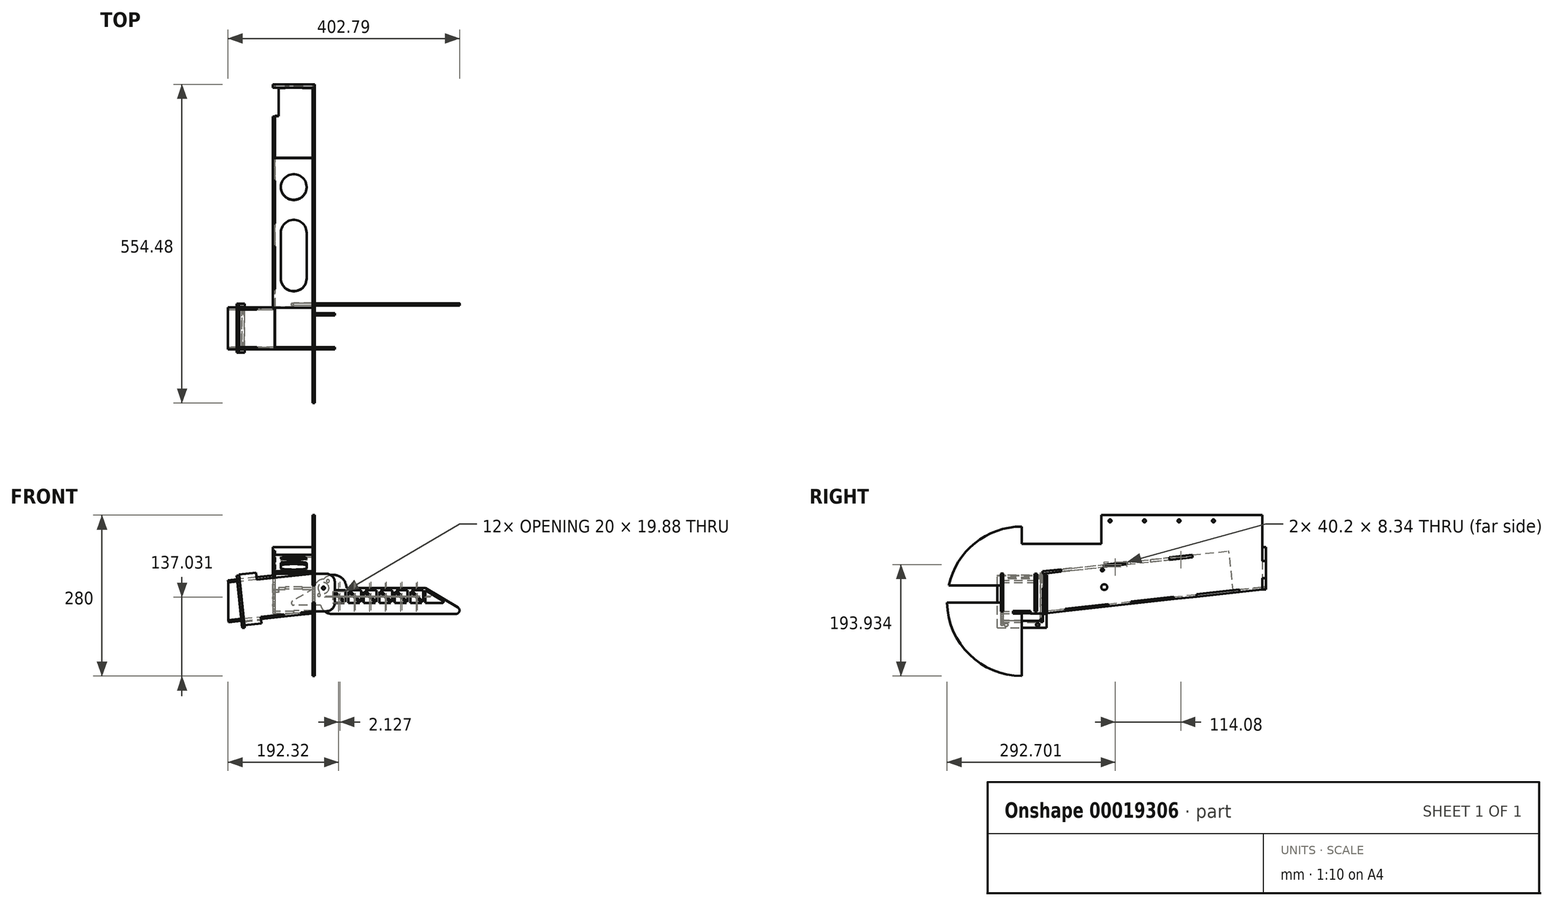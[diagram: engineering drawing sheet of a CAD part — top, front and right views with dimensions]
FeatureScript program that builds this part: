
annotation { "Feature Type Name" : "Feature", "Feature Type Description" : "" }
export const myFeature = defineFeature(function(context is Context, id is Id, definition is map)
    precondition{}
    {
        {
            var Q0;
            Q0=qCreatedBy(makeId("Front.planeOp"),FACE);
            var sketch = newSketch(context, id + "F0", { "sketchPlane" : qUnion([Q0])});
            skCircle(sketch, "E0", {"center": v(0, 0) * mm, "radius": 150 * mm, "construction": true});
            skLineSegment(sketch, "E1", {"start": v(0, 150) * mm, "end": v(0, -150) * mm, "construction": true});
            skSolve(sketch);
        }
        {
            var Q0;
            Q0=qCreatedBy(makeId("Front.planeOp"),FACE);
            var sketch = newSketch(context, id + "F1", { "sketchPlane" : qUnion([Q0])});
            skLineSegment(sketch, "E2", {"start": v(-146.4, 32.68) * mm, "end": v(-146.4, -32.68) * mm});
            skLineSegment(sketch, "E3", {"start": v(-146.4, -32.68) * mm, "end": v(-119.71, -29.87) * mm});
            skLineSegment(sketch, "E4", {"start": v(0, -17.3) * mm, "end": v(0, -2.3) * mm});
            skLineSegment(sketch, "E5", {"start": v(0, 48.07) * mm, "end": v(-96.67, 37.9) * mm});
            skLineSegment(sketch, "E6.bottom", {"start": v(0, -17.3) * mm, "end": v(-73, -17.3) * mm, "construction": true});
            skLineSegment(sketch, "E6.top", {"start": v(0, 48.07) * mm, "end": v(-73, 48.07) * mm, "construction": true});
            skLineSegment(sketch, "E6.left", {"start": v(0, -17.3) * mm, "end": v(0, 48.07) * mm, "construction": true});
            skLineSegment(sketch, "E6.right", {"start": v(-73, -17.3) * mm, "end": v(-73, 48.07) * mm, "construction": true});
            skLineSegment(sketch, "E7", {"start": v(-119.71, -29.87) * mm, "end": v(-118.46, -41.8) * mm});
            skLineSegment(sketch, "E8", {"start": v(-118.46, -41.8) * mm, "end": v(-88.62, -38.67) * mm});
            skLineSegment(sketch, "E9", {"start": v(-88.62, -38.67) * mm, "end": v(-89.88, -26.74) * mm});
            skLineSegment(sketch, "E10", {"start": v(-49.73, -22.52) * mm, "end": v(-49.3, -26.5) * mm});
            skLineSegment(sketch, "E11", {"start": v(-49.3, -26.5) * mm, "end": v(-19.47, -23.36) * mm});
            skLineSegment(sketch, "E12", {"start": v(-19.47, -23.36) * mm, "end": v(-19.9, -19.38) * mm});
            skLineSegment(sketch, "E13", {"start": v(-126.5, 34.77) * mm, "end": v(-127.76, 46.7) * mm});
            skLineSegment(sketch, "E14", {"start": v(-127.76, 46.7) * mm, "end": v(-97.93, 49.84) * mm});
            skLineSegment(sketch, "E15", {"start": v(-97.93, 49.84) * mm, "end": v(-96.67, 37.9) * mm});
            skLineSegment(sketch, "E16", {"start": v(0, 27.7) * mm, "end": v(4, 27.7) * mm});
            skLineSegment(sketch, "E17", {"start": v(4, -2.3) * mm, "end": v(0, -2.3) * mm});
            skLineSegment(sketch, "E18", {"start": v(-146.4, 32.68) * mm, "end": v(-139.6, -31.96) * mm, "construction": true});
            skLineSegment(sketch, "E19.trimOffspring", {"start": v(-89.88, -26.74) * mm, "end": v(-49.73, -22.52) * mm});
            skLineSegment(sketch, "E20.trimOffspring", {"start": v(-126.5, 34.77) * mm, "end": v(-146.4, 32.68) * mm});
            skLineSegment(sketch, "E21.trimOffspring", {"start": v(-19.9, -19.38) * mm, "end": v(0, -17.3) * mm});
            skLineSegment(sketch, "E22.trimOffspring", {"start": v(0, 27.7) * mm, "end": v(0, 48.07) * mm});
            skLineSegment(sketch, "E23.bottom", {"start": v(4, 48.07) * mm, "end": v(24, 48.07) * mm});
            skLineSegment(sketch, "E23.top", {"start": v(4, -17.3) * mm, "end": v(24, -17.3) * mm});
            skLineSegment(sketch, "E23.left", {"start": v(4, 48.07) * mm, "end": v(4, 27.7) * mm});
            skLineSegment(sketch, "E23.right", {"start": v(39, 33.07) * mm, "end": v(39, -2.3) * mm});
            skLineSegment(sketch, "E24.trimOffspring", {"start": v(4, -2.3) * mm, "end": v(4, -17.3) * mm});
            skCircle(sketch, "E25", {"center": v(19.25, 23.09) * mm, "radius": 2.5 * mm});
            skPoint(sketch, "E26.visualSharp", {"position": v(39, 48.07) * mm});
            skArc(sketch, "E26.filletArc", {"start": v(39, 33.07) * mm, "mid": v(34.6, 43.67) * mm, "end": v(24, 48.07) * mm});
            skPoint(sketch, "E27.visualSharp", {"position": v(39, -17.3) * mm});
            skArc(sketch, "E27.filletArc", {"start": v(24, -17.3) * mm, "mid": v(34.6, -12.9) * mm, "end": v(39, -2.3) * mm});
            skSolve(sketch);
        }
        {
            var Q0;
            Q0=qSketchRegion(id+"F1",true);
            extrude(context, id + "F2", {"entities" : qUnion([Q0]), "depth" : 4 * mm});
        }
        {
            var Q0;
            Q0=makeQuery(id+"F2.opExtrude","SWEPT_FACE",FACE,{"disambiguationData":[OSD([sQuery(id+"F1.wireOp",EDGE,"E3")])]});
            var sketch = newSketch(context, id + "F3", { "sketchPlane" : qUnion([Q0])});
            skLineSegment(sketch, "E28.bottom", {"start": v(-149.01, 4) * mm, "end": v(-122.18, 4) * mm});
            skLineSegment(sketch, "E28.top", {"start": v(-149.01, -69) * mm, "end": v(-122.18, -69) * mm});
            skLineSegment(sketch, "E28.left", {"start": v(-149.01, 4) * mm, "end": v(-149.01, -69) * mm});
            skLineSegment(sketch, "E28.right", {"start": v(-1.8, 4) * mm, "end": v(-1.8, -17.5) * mm});
            skLineSegment(sketch, "E29", {"start": v(-122.18, 4) * mm, "end": v(-122.18, 0) * mm});
            skLineSegment(sketch, "E30", {"start": v(-122.18, 0) * mm, "end": v(-92.18, 0) * mm});
            skLineSegment(sketch, "E31", {"start": v(-92.18, 0) * mm, "end": v(-92.18, 4) * mm});
            skLineSegment(sketch, "E32.0.0", {"start": v(-51.8, 0) * mm, "end": v(-21.8, 0) * mm});
            skLineSegment(sketch, "E32.0.1", {"start": v(-21.8, 0) * mm, "end": v(-21.8, 4) * mm});
            skLineSegment(sketch, "E32.0.3", {"start": v(-51.8, 4) * mm, "end": v(-51.8, 0) * mm});
            skLineSegment(sketch, "E33.trimOffspring", {"start": v(-21.8, 4) * mm, "end": v(-1.8, 4) * mm});
            skLineSegment(sketch, "E34.trimOffspring", {"start": v(-92.18, 4) * mm, "end": v(-51.8, 4) * mm});
            skLineSegment(sketch, "E35", {"start": v(-1.8, -17.5) * mm, "end": v(2.2, -17.5) * mm});
            skLineSegment(sketch, "E36", {"start": v(2.2, -17.5) * mm, "end": v(2.2, -47.5) * mm});
            skLineSegment(sketch, "E37", {"start": v(2.2, -47.5) * mm, "end": v(-1.8, -47.5) * mm});
            skLineSegment(sketch, "E38.trimOffspring", {"start": v(-1.8, -47.5) * mm, "end": v(-1.8, -69) * mm});
            skLineSegment(sketch, "E39", {"start": v(-122.18, -69) * mm, "end": v(-122.18, -65) * mm});
            skLineSegment(sketch, "E40", {"start": v(-122.18, -65) * mm, "end": v(-92.18, -65) * mm});
            skLineSegment(sketch, "E41", {"start": v(-92.18, -65) * mm, "end": v(-92.18, -69) * mm});
            skLineSegment(sketch, "E42.trimOffspring", {"start": v(-92.18, -69) * mm, "end": v(-1.8, -69) * mm});
            skSolve(sketch);
        }
        {
            var Q0;
            Q0=qSketchRegion(id+"F3",true);
            extrude(context, id + "F4", {"entities" : qUnion([Q0]), "depth" : 4 * mm});
        }
        {
            var Q0;
            Q0=makeQuery(id+"F2.opExtrude","SWEPT_FACE",FACE,{"disambiguationData":[OSD([sQuery(id+"F1.wireOp",EDGE,"E22.trimOffspring")])]});
            var sketch = newSketch(context, id + "F5", { "sketchPlane" : qUnion([Q0])});
            skLineSegment(sketch, "E43", {"start": v(451, 20.66) * mm, "end": v(451, 40.33) * mm});
            skLineSegment(sketch, "E44", {"start": v(451, 90) * mm, "end": v(403.72, 84.8) * mm});
            skLineSegment(sketch, "E45", {"start": v(69, 48.07) * mm, "end": v(-4, 48.07) * mm, "construction": true});
            skLineSegment(sketch, "E46", {"start": v(-4, 27.7) * mm, "end": v(0, 27.7) * mm});
            skLineSegment(sketch, "E47", {"start": v(0, 27.7) * mm, "end": v(0, -2.3) * mm});
            skLineSegment(sketch, "E48", {"start": v(0, -2.3) * mm, "end": v(-4, -2.3) * mm});
            skLineSegment(sketch, "E49", {"start": v(17.5, -21.27) * mm, "end": v(17.5, -16.87) * mm});
            skLineSegment(sketch, "E50", {"start": v(17.5, -16.87) * mm, "end": v(47.5, -16.87) * mm});
            skLineSegment(sketch, "E51", {"start": v(47.5, -16.87) * mm, "end": v(47.5, -21.27) * mm});
            skLineSegment(sketch, "E52", {"start": v(47.5, -21.27) * mm, "end": v(69, -21.27) * mm});
            skLineSegment(sketch, "E53", {"start": v(32.5, 48.07) * mm, "end": v(32.5, -16.87) * mm, "construction": true});
            skCircle(sketch, "E54", {"center": v(32.5, 0) * mm, "radius": 150 * mm, "construction": true});
            skLineSegment(sketch, "E55", {"start": v(-117.5, 0) * mm, "end": v(-117.5, -150) * mm, "construction": true});
            skLineSegment(sketch, "E56", {"start": v(-117.5, -150) * mm, "end": v(451, -150) * mm, "construction": true});
            skLineSegment(sketch, "E57", {"start": v(451, -150) * mm, "end": v(451, 150) * mm, "construction": true});
            skLineSegment(sketch, "E58", {"start": v(451, 150) * mm, "end": v(-117.5, 150) * mm, "construction": true});
            skLineSegment(sketch, "E59", {"start": v(-117.5, 0) * mm, "end": v(-117.5, 150) * mm, "construction": true});
            skLineSegment(sketch, "E60", {"start": v(451, 70.33) * mm, "end": v(457, 70.33) * mm});
            skLineSegment(sketch, "E61", {"start": v(457, 70.33) * mm, "end": v(457, 40.33) * mm});
            skLineSegment(sketch, "E62", {"start": v(457, 40.33) * mm, "end": v(451, 40.33) * mm});
            skLineSegment(sketch, "E63.trimOffspring", {"start": v(451, 70.33) * mm, "end": v(451, 90) * mm});
            skLineSegment(sketch, "E64", {"start": v(108.76, -16.9) * mm, "end": v(108.32, -12.93) * mm});
            skLineSegment(sketch, "E65", {"start": v(108.32, -12.93) * mm, "end": v(182.64, -4.77) * mm});
            skLineSegment(sketch, "E66", {"start": v(182.64, -4.77) * mm, "end": v(183.08, -8.75) * mm});
            skLineSegment(sketch, "E67", {"start": v(222.84, -4.38) * mm, "end": v(222.4, -0.4) * mm});
            skLineSegment(sketch, "E68", {"start": v(222.4, -0.4) * mm, "end": v(296.72, 7.75) * mm});
            skLineSegment(sketch, "E69", {"start": v(296.72, 7.75) * mm, "end": v(297.16, 3.78) * mm});
            skLineSegment(sketch, "E70", {"start": v(336.92, 8.14) * mm, "end": v(336.48, 12.12) * mm});
            skLineSegment(sketch, "E71", {"start": v(336.48, 12.12) * mm, "end": v(410.8, 20.28) * mm});
            skLineSegment(sketch, "E72", {"start": v(410.8, 20.28) * mm, "end": v(411.24, 16.3) * mm});
            skLineSegment(sketch, "E73.trimOffspring", {"start": v(183.08, -8.75) * mm, "end": v(222.84, -4.38) * mm});
            skLineSegment(sketch, "E74.trimOffspring", {"start": v(411.24, 16.3) * mm, "end": v(451, 20.66) * mm});
            skLineSegment(sketch, "E75", {"start": v(108.76, -16.9) * mm, "end": v(76, -20.5) * mm});
            skLineSegment(sketch, "E76.trimOffspring", {"start": v(297.16, 3.78) * mm, "end": v(336.92, 8.14) * mm});
            skLineSegment(sketch, "E77", {"start": v(101.24, 51.6) * mm, "end": v(100.8, 55.58) * mm});
            skLineSegment(sketch, "E78", {"start": v(100.8, 55.58) * mm, "end": v(175.12, 63.74) * mm, "construction": true});
            skLineSegment(sketch, "E79", {"start": v(175.12, 63.74) * mm, "end": v(175.56, 59.76) * mm});
            skLineSegment(sketch, "E80", {"start": v(215.32, 64.13) * mm, "end": v(214.88, 68.1) * mm});
            skLineSegment(sketch, "E81", {"start": v(214.88, 68.1) * mm, "end": v(289.2, 76.26) * mm, "construction": true});
            skLineSegment(sketch, "E82", {"start": v(289.2, 76.26) * mm, "end": v(289.64, 72.29) * mm});
            skLineSegment(sketch, "E83", {"start": v(329.4, 76.65) * mm, "end": v(328.96, 80.63) * mm});
            skLineSegment(sketch, "E84", {"start": v(328.96, 80.63) * mm, "end": v(403.28, 88.79) * mm, "construction": true});
            skLineSegment(sketch, "E85", {"start": v(403.28, 88.79) * mm, "end": v(403.72, 84.8) * mm});
            skLineSegment(sketch, "E86.trimOffspring", {"start": v(101.24, 51.6) * mm, "end": v(69, 48.07) * mm});
            skLineSegment(sketch, "E87.trimOffspring", {"start": v(215.32, 64.13) * mm, "end": v(175.56, 59.76) * mm});
            skLineSegment(sketch, "E88.trimOffspring", {"start": v(329.4, 76.65) * mm, "end": v(289.64, 72.29) * mm});
            skLineSegment(sketch, "E89.bottom", {"start": v(69, 22.81) * mm, "end": v(76, 22.81) * mm});
            skLineSegment(sketch, "E89.top", {"start": v(69, -7.19) * mm, "end": v(76, -7.19) * mm, "construction": true});
            skLineSegment(sketch, "E89.left", {"start": v(69, 22.81) * mm, "end": v(69, -7.19) * mm});
            skLineSegment(sketch, "E89.right", {"start": v(76, 22.81) * mm, "end": v(76, -7.19) * mm});
            skLineSegment(sketch, "E90", {"start": v(76, -7.19) * mm, "end": v(76, -20.5) * mm});
            skLineSegment(sketch, "E91", {"start": v(69, -7.19) * mm, "end": v(69, -21.27) * mm});
            skLineSegment(sketch, "E92.trimOffspring", {"start": v(69, -21.27) * mm, "end": v(69, -21.27) * mm});
            skLineSegment(sketch, "E93", {"start": v(451, 90) * mm, "end": v(451, 150) * mm});
            skLineSegment(sketch, "E94", {"start": v(451, 150) * mm, "end": v(-4, 150) * mm, "construction": true});
            skLineSegment(sketch, "E95", {"start": v(-4, 48.07) * mm, "end": v(-4, 150) * mm, "construction": true});
            skLineSegment(sketch, "E96", {"start": v(175.12, 63.74) * mm, "end": v(214.88, 68.1) * mm});
            skLineSegment(sketch, "E97", {"start": v(289.2, 76.26) * mm, "end": v(328.96, 80.63) * mm});
            skLineSegment(sketch, "E98", {"start": v(403.28, 88.79) * mm, "end": v(451, 94.02) * mm});
            skLineSegment(sketch, "E99", {"start": v(69, 48.07) * mm, "end": v(68.56, 52.04) * mm});
            skLineSegment(sketch, "E100", {"start": v(68.56, 52.04) * mm, "end": v(100.8, 55.58) * mm});
            skCircle(sketch, "E101", {"center": v(66, 140) * mm, "radius": 2.5 * mm, "construction": true});
            skCircle(sketch, "E102", {"center": v(126, 140) * mm, "radius": 2.5 * mm, "construction": true});
            skCircle(sketch, "E103", {"center": v(186, 140) * mm, "radius": 2.5 * mm});
            skCircle(sketch, "E104", {"center": v(246, 140) * mm, "radius": 2.5 * mm});
            skCircle(sketch, "E105", {"center": v(306, 140) * mm, "radius": 2.5 * mm});
            skCircle(sketch, "E106", {"center": v(366, 140) * mm, "radius": 2.5 * mm});
            skCircle(sketch, "E107", {"center": v(421, 120) * mm, "radius": 30 * mm, "construction": true});
            skLineSegment(sketch, "E108.bottom", {"start": v(55, 40.73) * mm, "end": v(59, 40.73) * mm});
            skLineSegment(sketch, "E108.top", {"start": v(55, 20.73) * mm, "end": v(59, 20.73) * mm});
            skLineSegment(sketch, "E108.left", {"start": v(55, 40.73) * mm, "end": v(55, 20.73) * mm});
            skLineSegment(sketch, "E108.right", {"start": v(59, 40.73) * mm, "end": v(59, 20.73) * mm});
            skLineSegment(sketch, "E109.bottom", {"start": v(55, 12.73) * mm, "end": v(59, 12.73) * mm});
            skLineSegment(sketch, "E109.top", {"start": v(55, -7.27) * mm, "end": v(59, -7.27) * mm});
            skLineSegment(sketch, "E109.left", {"start": v(55, 12.73) * mm, "end": v(55, -7.27) * mm});
            skLineSegment(sketch, "E109.right", {"start": v(59, 12.73) * mm, "end": v(59, -7.27) * mm});
            skLineSegment(sketch, "E110", {"start": v(-4, 100) * mm, "end": v(171, 100) * mm});
            skLineSegment(sketch, "E111", {"start": v(171, 100) * mm, "end": v(171, 150) * mm});
            skLineSegment(sketch, "E112", {"start": v(171, 150) * mm, "end": v(451, 150) * mm});
            skArc(sketch, "E113", {"start": v(32.5, 130) * mm, "mid": v(-49.04, 101.25) * mm, "end": v(-94.51, 27.7) * mm});
            skLineSegment(sketch, "E114", {"start": v(32.5, 130) * mm, "end": v(32.5, -130) * mm, "construction": true});
            skLineSegment(sketch, "E115", {"start": v(32.5, 130) * mm, "end": v(32.5, 100) * mm});
            skLineSegment(sketch, "E116", {"start": v(32.5, -130) * mm, "end": v(32.5, -21.27) * mm});
            skLineSegment(sketch, "E117", {"start": v(32.5, -21.27) * mm, "end": v(17.5, -21.27) * mm});
            skLineSegment(sketch, "E118", {"start": v(-4, 27.7) * mm, "end": v(-94.51, 27.7) * mm});
            skLineSegment(sketch, "E119", {"start": v(-4, -2.3) * mm, "end": v(-97.48, -2.3) * mm});
            skArc(sketch, "E120.trimOffspring", {"start": v(-97.48, -2.3) * mm, "mid": v(-58.6, -92.73) * mm, "end": v(32.5, -130) * mm});
            skLineSegment(sketch, "E121", {"start": v(76, 13.7) * mm, "end": v(176, 24.68) * mm, "construction": true});
            skCircle(sketch, "E122", {"center": v(176, 24.68) * mm, "radius": 5 * mm});
            skLineSegment(sketch, "E123", {"start": v(172.73, 54.5) * mm, "end": v(176, 24.68) * mm, "construction": true});
            skCircle(sketch, "E124", {"center": v(172.73, 54.5) * mm, "radius": 2.5 * mm});
            skSolve(sketch);
        }
        {
            var Q0;
            Q0=qSketchRegion(id+"F5",true);
            extrude(context, id + "F6", {"entities" : qUnion([Q0]), "depth" : 4 * mm});
        }
        {
            var Q0;
            Q0=makeQuery(id+"F6.opExtrude","SWEPT_FACE",FACE,{"disambiguationData":[OSD([sQuery(id+"F5.wireOp",EDGE,"E68")])]});
            var sketch = newSketch(context, id + "F7", { "sketchPlane" : qUnion([Q0])});
            skLineSegment(sketch, "E125", {"start": v(-65, -66.7) * mm, "end": v(-65, -106.27) * mm});
            skLineSegment(sketch, "E126", {"start": v(-65, -450.56) * mm, "end": v(-47.5, -450.56) * mm});
            skLineSegment(sketch, "E127", {"start": v(4, -410.56) * mm, "end": v(4, -335.8) * mm});
            skLineSegment(sketch, "E128.0.0", {"start": v(0, -410.56) * mm, "end": v(0, -450.56) * mm});
            skLineSegment(sketch, "E128.0.3", {"start": v(4, -410.56) * mm, "end": v(0, -410.56) * mm});
            skPoint(sketch, "E128.0.1.end.orphan", {"position": v(4, -450.56) * mm});
            skLineSegment(sketch, "E129.0.0", {"start": v(0, -295.8) * mm, "end": v(0, -335.8) * mm});
            skLineSegment(sketch, "E129.0.1", {"start": v(0, -335.8) * mm, "end": v(4, -335.8) * mm});
            skLineSegment(sketch, "E129.0.3", {"start": v(4, -295.8) * mm, "end": v(0, -295.8) * mm});
            skLineSegment(sketch, "E130.trimOffspring", {"start": v(4, -295.8) * mm, "end": v(4, -221.03) * mm});
            skLineSegment(sketch, "E131.0.0", {"start": v(0, -181.03) * mm, "end": v(0, -221.03) * mm});
            skLineSegment(sketch, "E131.0.1", {"start": v(0, -221.03) * mm, "end": v(4, -221.03) * mm});
            skLineSegment(sketch, "E131.0.3", {"start": v(4, -181.03) * mm, "end": v(0, -181.03) * mm});
            skLineSegment(sketch, "E132.trimOffspring", {"start": v(4, -181.03) * mm, "end": v(4, -106.27) * mm});
            skLineSegment(sketch, "E133.0.0", {"start": v(0, -66.7) * mm, "end": v(0, -67.8) * mm});
            skLineSegment(sketch, "E133.0.1", {"start": v(0, -106.27) * mm, "end": v(4, -106.27) * mm});
            skLineSegment(sketch, "E134", {"start": v(0, -66.7) * mm, "end": v(-65, -66.7) * mm});
            skLineSegment(sketch, "E135", {"start": v(-32.5, -450.56) * mm, "end": v(-32.5, -66.7) * mm, "construction": true});
            skLineSegment(sketch, "E136.0.MirrorCS", {"start": v(-65, -106.27) * mm, "end": v(-69, -106.27) * mm});
            skLineSegment(sketch, "E137.0.MirrorCS", {"start": v(-69, -181.03) * mm, "end": v(-69, -106.27) * mm});
            skLineSegment(sketch, "E138.0.MirrorCS", {"start": v(-69, -181.03) * mm, "end": v(-65, -181.03) * mm});
            skLineSegment(sketch, "E139.0.MirrorCS", {"start": v(-65, -221.03) * mm, "end": v(-69, -221.03) * mm});
            skLineSegment(sketch, "E140.0.MirrorCS", {"start": v(-69, -295.8) * mm, "end": v(-69, -221.03) * mm});
            skLineSegment(sketch, "E141.0.MirrorCS", {"start": v(-69, -295.8) * mm, "end": v(-65, -295.8) * mm});
            skLineSegment(sketch, "E142.0.MirrorCS", {"start": v(-65, -335.8) * mm, "end": v(-69, -335.8) * mm});
            skLineSegment(sketch, "E143.0.MirrorCS", {"start": v(-69, -396.56) * mm, "end": v(-69, -335.8) * mm});
            skLineSegment(sketch, "E144.trimOffspring", {"start": v(-65, -181.03) * mm, "end": v(-65, -221.03) * mm});
            skLineSegment(sketch, "E145.trimOffspring", {"start": v(-65, -295.8) * mm, "end": v(-65, -335.8) * mm});
            skLineSegment(sketch, "E146.trimOffspring", {"start": v(-65, -440.56) * mm, "end": v(-65, -450.56) * mm});
            skLineSegment(sketch, "E147", {"start": v(-17.5, -450.56) * mm, "end": v(-17.5, -454.56) * mm});
            skLineSegment(sketch, "E148", {"start": v(-17.5, -454.56) * mm, "end": v(-47.5, -454.56) * mm});
            skLineSegment(sketch, "E149", {"start": v(-47.5, -454.56) * mm, "end": v(-47.5, -450.56) * mm});
            skLineSegment(sketch, "E150.trimOffspring", {"start": v(-17.5, -450.56) * mm, "end": v(0, -450.56) * mm});
            skLineSegment(sketch, "E151.bottom", {"start": v(0, -67.8) * mm, "end": v(-32.5, -67.8) * mm});
            skLineSegment(sketch, "E151.top", {"start": v(0, -73.8) * mm, "end": v(-32.5, -73.8) * mm});
            skLineSegment(sketch, "E151.right", {"start": v(-32.5, -67.8) * mm, "end": v(-32.5, -73.8) * mm});
            skLineSegment(sketch, "E152.trimOffspring", {"start": v(0, -73.8) * mm, "end": v(0, -106.27) * mm});
            skLineSegment(sketch, "E153", {"start": v(-65, -401.56) * mm, "end": v(-65, -396.56) * mm});
            skLineSegment(sketch, "E154", {"start": v(-65, -396.56) * mm, "end": v(-69, -396.56) * mm});
            skPoint(sketch, "E155.orphan", {"position": v(-69, -410.56) * mm});
            skLineSegment(sketch, "E156", {"start": v(-65, -440.56) * mm, "end": v(-59, -440.56) * mm});
            skLineSegment(sketch, "E157", {"start": v(-59, -440.56) * mm, "end": v(-59, -401.56) * mm});
            skLineSegment(sketch, "E158", {"start": v(-59, -401.56) * mm, "end": v(-65, -401.56) * mm});
            skPoint(sketch, "E159.orphan", {"position": v(-65, -410.56) * mm});
            skLineSegment(sketch, "E160", {"start": v(-65, -440.56) * mm, "end": v(-65, -401.56) * mm, "construction": true});
            skSolve(sketch);
        }
        {
            var Q0;
            Q0=qSketchRegion(id+"F7",true);
            extrude(context, id + "F8", {"entities" : qUnion([Q0]), "depth" : 4 * mm});
        }
        {
            var Q0;
            Q0=makeQuery(id+"F8.opExtrude","SWEPT_FACE",FACE,{"disambiguationData":[OSD([sQuery(id+"F7.wireOp",EDGE,"E146.trimOffspring")])]});
            var sketch = newSketch(context, id + "F9", { "sketchPlane" : qUnion([Q0])});
            skLineSegment(sketch, "E161.0.0", {"start": v(-451, 20.66) * mm, "end": v(-442.05, 19.68) * mm});
            skLineSegment(sketch, "E161.0.3", {"start": v(-336.48, 12.12) * mm, "end": v(-336.92, 8.14) * mm});
            skLineSegment(sketch, "E161.0.4", {"start": v(-336.92, 8.14) * mm, "end": v(-297.16, 3.78) * mm});
            skLineSegment(sketch, "E161.0.5", {"start": v(-297.16, 3.78) * mm, "end": v(-296.72, 7.75) * mm});
            skLineSegment(sketch, "E161.0.6", {"start": v(-296.72, 7.75) * mm, "end": v(-222.4, -0.4) * mm});
            skLineSegment(sketch, "E161.0.7", {"start": v(-222.4, -0.4) * mm, "end": v(-222.84, -4.38) * mm});
            skLineSegment(sketch, "E161.0.8", {"start": v(-222.84, -4.38) * mm, "end": v(-183.08, -8.75) * mm});
            skLineSegment(sketch, "E161.0.9", {"start": v(-183.08, -8.75) * mm, "end": v(-182.64, -4.77) * mm});
            skLineSegment(sketch, "E161.0.10", {"start": v(-182.64, -4.77) * mm, "end": v(-108.32, -12.93) * mm});
            skLineSegment(sketch, "E161.0.11", {"start": v(-108.32, -12.93) * mm, "end": v(-108.76, -16.9) * mm});
            skLineSegment(sketch, "E161.0.12", {"start": v(-108.76, -16.9) * mm, "end": v(-69, -21.27) * mm});
            skLineSegment(sketch, "E161.0.24", {"start": v(-69, 48.07) * mm, "end": v(-101.24, 51.6) * mm});
            skLineSegment(sketch, "E161.0.25", {"start": v(-100.8, 55.58) * mm, "end": v(-101.24, 51.6) * mm});
            skLineSegment(sketch, "E161.0.26", {"start": v(-100.8, 55.58) * mm, "end": v(-175.12, 63.74) * mm});
            skLineSegment(sketch, "E161.0.27", {"start": v(-175.12, 63.74) * mm, "end": v(-175.56, 59.76) * mm});
            skLineSegment(sketch, "E161.0.28", {"start": v(-175.56, 59.76) * mm, "end": v(-215.32, 64.13) * mm});
            skLineSegment(sketch, "E161.0.29", {"start": v(-214.88, 68.1) * mm, "end": v(-215.32, 64.13) * mm});
            skLineSegment(sketch, "E161.0.30", {"start": v(-214.88, 68.1) * mm, "end": v(-289.2, 76.26) * mm});
            skLineSegment(sketch, "E161.0.31", {"start": v(-289.2, 76.26) * mm, "end": v(-289.64, 72.29) * mm});
            skLineSegment(sketch, "E161.0.32", {"start": v(-289.64, 72.29) * mm, "end": v(-329.4, 76.65) * mm});
            skLineSegment(sketch, "E161.0.33", {"start": v(-328.96, 80.63) * mm, "end": v(-329.4, 76.65) * mm});
            skLineSegment(sketch, "E161.0.34", {"start": v(-328.96, 80.63) * mm, "end": v(-392.84, 87.64) * mm});
            skLineSegment(sketch, "E161.0.37", {"start": v(-451, 94.02) * mm, "end": v(-451, 70.33) * mm});
            skLineSegment(sketch, "E161.0.38", {"start": v(-451, 70.33) * mm, "end": v(-457, 70.33) * mm});
            skLineSegment(sketch, "E161.0.39", {"start": v(-457, 70.33) * mm, "end": v(-457, 40.33) * mm});
            skLineSegment(sketch, "E161.0.40", {"start": v(-457, 40.33) * mm, "end": v(-451, 40.33) * mm});
            skLineSegment(sketch, "E161.0.41", {"start": v(-451, 40.33) * mm, "end": v(-451, 20.66) * mm});
            skLineSegment(sketch, "E162", {"start": v(-69, 45.23) * mm, "end": v(-69, 32.95) * mm});
            skLineSegment(sketch, "E163", {"start": v(-69, 32.95) * mm, "end": v(-65, 32.95) * mm});
            skLineSegment(sketch, "E164", {"start": v(-65, 32.95) * mm, "end": v(-65, 20.95) * mm});
            skLineSegment(sketch, "E165", {"start": v(-65, 20.95) * mm, "end": v(-69, 20.95) * mm});
            skLineSegment(sketch, "E166", {"start": v(-69, 5.84) * mm, "end": v(-65, 5.84) * mm});
            skLineSegment(sketch, "E167", {"start": v(-65, 5.84) * mm, "end": v(-65, -6.16) * mm});
            skLineSegment(sketch, "E168", {"start": v(-65, -6.16) * mm, "end": v(-69, -6.16) * mm});
            skLineSegment(sketch, "E169.trimOffspring", {"start": v(-69, 20.95) * mm, "end": v(-69, 5.84) * mm});
            skLineSegment(sketch, "E170.trimOffspring", {"start": v(-69, -6.16) * mm, "end": v(-69, -21.27) * mm});
            skCircle(sketch, "E171", {"center": v(-421, 51.44) * mm, "radius": 30 * mm, "construction": true});
            skLineSegment(sketch, "E172", {"start": v(-451, 94.02) * mm, "end": v(-442.05, 19.68) * mm});
            skLineSegment(sketch, "E173", {"start": v(-400.8, 15.15) * mm, "end": v(-392.84, 87.64) * mm});
            skLineSegment(sketch, "E174", {"start": v(-421, 17.37) * mm, "end": v(-421, 81.44) * mm, "construction": true});
            skPoint(sketch, "E161.0.35.end.orphan", {"position": v(-356.78, 84.6) * mm});
            skPoint(sketch, "E161.0.35.start.orphan", {"position": v(-355.76, 83.57) * mm});
            skLineSegment(sketch, "E175", {"start": v(-69, 48.07) * mm, "end": v(-67, 48.07) * mm});
            skLineSegment(sketch, "E176", {"start": v(-67, 48.07) * mm, "end": v(-67, 45.23) * mm});
            skLineSegment(sketch, "E177", {"start": v(-67, 45.23) * mm, "end": v(-69, 45.23) * mm});
            skLineSegment(sketch, "E178", {"start": v(-69, 32.95) * mm, "end": v(-69, 48.07) * mm, "construction": true});
            skLineSegment(sketch, "E179", {"start": v(-400.8, 15.15) * mm, "end": v(-397.32, 14.77) * mm});
            skLineSegment(sketch, "E180", {"start": v(-397.32, 14.77) * mm, "end": v(-396.89, 18.75) * mm});
            skLineSegment(sketch, "E181", {"start": v(-396.89, 18.75) * mm, "end": v(-336.48, 12.12) * mm});
            skPoint(sketch, "E182.trimOffspring.end.orphan", {"position": v(-411.24, 16.3) * mm});
            skCircle(sketch, "E183.0", {"center": v(-176, 24.68) * mm, "radius": 5 * mm});
            skCircle(sketch, "E183.1", {"center": v(-172.73, 54.5) * mm, "radius": 2.5 * mm});
            skSolve(sketch);
        }
        {
            var Q0;
            Q0=qSketchRegion(id+"F9",true);
            extrude(context, id + "F10", {"entities" : qUnion([Q0]), "depth" : 4 * mm});
        }
        {
            var Q0;
            Q0=makeQuery(id+"F4.opExtrude","SWEPT_FACE",FACE,{"disambiguationData":[OSD([sQuery(id+"F3.wireOp",EDGE,"E28.top")])]});
            var sketch = newSketch(context, id + "F11", { "sketchPlane" : qUnion([Q0])});
            skLineSegment(sketch, "E184", {"start": v(146.4, -32.68) * mm, "end": v(146.4, 32.68) * mm});
            skLineSegment(sketch, "E185", {"start": v(146.4, 32.68) * mm, "end": v(126.5, 34.77) * mm});
            skLineSegment(sketch, "E186", {"start": v(126.5, 34.77) * mm, "end": v(127.76, 46.7) * mm});
            skLineSegment(sketch, "E187", {"start": v(127.76, 46.7) * mm, "end": v(97.93, 49.84) * mm});
            skLineSegment(sketch, "E188", {"start": v(96.67, 37.9) * mm, "end": v(97.93, 49.84) * mm});
            skLineSegment(sketch, "E189", {"start": v(96.67, 37.9) * mm, "end": v(65, 41.23) * mm});
            skLineSegment(sketch, "E190", {"start": v(65, 41.23) * mm, "end": v(65, 32.95) * mm});
            skLineSegment(sketch, "E191", {"start": v(65, 32.95) * mm, "end": v(69, 32.95) * mm});
            skLineSegment(sketch, "E192", {"start": v(69, 32.95) * mm, "end": v(69, 20.95) * mm});
            skLineSegment(sketch, "E193", {"start": v(69, 20.95) * mm, "end": v(65, 20.95) * mm});
            skLineSegment(sketch, "E194", {"start": v(65, 20.95) * mm, "end": v(65, 5.84) * mm});
            skLineSegment(sketch, "E195", {"start": v(65, 5.84) * mm, "end": v(69, 5.84) * mm});
            skLineSegment(sketch, "E196", {"start": v(69, 5.84) * mm, "end": v(69, -6.16) * mm});
            skLineSegment(sketch, "E197", {"start": v(69, -6.16) * mm, "end": v(65, -6.16) * mm});
            skLineSegment(sketch, "E198", {"start": v(65, -6.16) * mm, "end": v(65, -24.12) * mm});
            skLineSegment(sketch, "E199", {"start": v(146.4, -32.68) * mm, "end": v(119.71, -29.87) * mm});
            skLineSegment(sketch, "E200", {"start": v(89.25, -32.7) * mm, "end": v(89.88, -26.74) * mm});
            skLineSegment(sketch, "E201", {"start": v(89.88, -26.74) * mm, "end": v(65, -24.12) * mm});
            skLineSegment(sketch, "E202", {"start": v(119.71, -29.87) * mm, "end": v(119.09, -35.84) * mm});
            skLineSegment(sketch, "E203", {"start": v(119.09, -35.84) * mm, "end": v(89.25, -32.7) * mm});
            skSolve(sketch);
        }
        {
            var Q0;
            Q0=qSketchRegion(id+"F11",true);
            extrude(context, id + "F12", {"entities" : qUnion([Q0]), "oppositeDirection" : true, "depth" : 4 * mm});
        }
        {
            var Q0;
            Q0=makeQuery(id+"F12.opExtrude","SWEPT_FACE",FACE,{"disambiguationData":[OSD([sQuery(id+"F11.wireOp",EDGE,"E185")])]});
            var sketch = newSketch(context, id + "F13", { "sketchPlane" : qUnion([Q0])});
            skLineSegment(sketch, "E204.bottom", {"start": v(-142.18, 69) * mm, "end": v(-122.18, 69) * mm});
            skLineSegment(sketch, "E204.top", {"start": v(-142.18, -4) * mm, "end": v(-122.18, -4) * mm});
            skLineSegment(sketch, "E204.left", {"start": v(-142.18, 69) * mm, "end": v(-142.18, -4) * mm});
            skLineSegment(sketch, "E204.right", {"start": v(-60.33, 69) * mm, "end": v(-60.33, -4) * mm});
            skLineSegment(sketch, "E205.0.1", {"start": v(-122.18, 69) * mm, "end": v(-122.18, 65) * mm});
            skLineSegment(sketch, "E205.0.2", {"start": v(-122.18, 65) * mm, "end": v(-92.18, 65) * mm});
            skLineSegment(sketch, "E205.0.3", {"start": v(-92.18, 65) * mm, "end": v(-92.18, 69) * mm});
            skLineSegment(sketch, "E206.0.0", {"start": v(-92.18, 0) * mm, "end": v(-122.18, 0) * mm});
            skLineSegment(sketch, "E206.0.1", {"start": v(-122.18, 0) * mm, "end": v(-122.18, -4) * mm});
            skLineSegment(sketch, "E206.0.3", {"start": v(-92.18, -4) * mm, "end": v(-92.18, 0) * mm});
            skLineSegment(sketch, "E207.trimOffspring", {"start": v(-92.18, 69) * mm, "end": v(-60.33, 69) * mm});
            skLineSegment(sketch, "E208.trimOffspring", {"start": v(-92.18, -4) * mm, "end": v(-60.33, -4) * mm});
            skSolve(sketch);
        }
        {
            var Q0;
            Q0=qSketchRegion(id+"F13",true);
            extrude(context, id + "F14", {"entities" : qUnion([Q0]), "depth" : 4 * mm});
        }
        {
            var Q0;
            Q0=makeQuery(id+"F10.opExtrude","SWEPT_FACE",FACE,{"disambiguationData":[OSD([sQuery(id+"F9.wireOp",EDGE,"E161.0.41")])]});
            var sketch = newSketch(context, id + "F15", { "sketchPlane" : qUnion([Q0])});
            skLineSegment(sketch, "E209.bottom", {"start": v(69, 20.66) * mm, "end": v(47.5, 20.66) * mm});
            skLineSegment(sketch, "E209.left", {"start": v(69, 20.66) * mm, "end": v(69, 40.33) * mm});
            skLineSegment(sketch, "E209.right", {"start": v(-4, 20.66) * mm, "end": v(-4, 40.33) * mm});
            skLineSegment(sketch, "E210.0.0", {"start": v(0, 40.33) * mm, "end": v(0, 70.33) * mm});
            skLineSegment(sketch, "E210.0.3", {"start": v(-4, 40.33) * mm, "end": v(0, 40.33) * mm});
            skLineSegment(sketch, "E211.0.0", {"start": v(65, 70.33) * mm, "end": v(65, 40.33) * mm});
            skLineSegment(sketch, "E211.0.1", {"start": v(65, 40.33) * mm, "end": v(69, 40.33) * mm});
            skLineSegment(sketch, "E212", {"start": v(17.5, 20.66) * mm, "end": v(17.5, 25.08) * mm});
            skLineSegment(sketch, "E213", {"start": v(17.5, 25.08) * mm, "end": v(47.5, 25.08) * mm});
            skLineSegment(sketch, "E214", {"start": v(47.5, 25.08) * mm, "end": v(47.5, 20.66) * mm});
            skLineSegment(sketch, "E215.trimOffspring", {"start": v(17.5, 20.66) * mm, "end": v(-4, 20.66) * mm});
            skLineSegment(sketch, "E216", {"start": v(0, 70.33) * mm, "end": v(-4, 70.33) * mm});
            skLineSegment(sketch, "E217", {"start": v(-4, 70.33) * mm, "end": v(-4, 94.02) * mm});
            skLineSegment(sketch, "E218", {"start": v(-4, 94.02) * mm, "end": v(69, 94.02) * mm});
            skLineSegment(sketch, "E219", {"start": v(69, 94.02) * mm, "end": v(69, 70.33) * mm});
            skLineSegment(sketch, "E220", {"start": v(69, 70.33) * mm, "end": v(65, 70.33) * mm});
            skSolve(sketch);
        }
        {
            var Q0;
            Q0=qSketchRegion(id+"F15",true);
            extrude(context, id + "F16", {"entities" : qUnion([Q0]), "depth" : 6 * mm});
        }
        {
            var Q0;
            Q0=makeQuery(id+"F6.opExtrude","SWEPT_FACE",FACE,{"disambiguationData":[OSD([sQuery(id+"F5.wireOp",EDGE,"E88.trimOffspring")])]});
            var sketch = newSketch(context, id + "F17", { "sketchPlane" : qUnion([Q0])});
            skLineSegment(sketch, "E221.bottom", {"start": v(4, 335.8) * mm, "end": v(-69, 335.8) * mm});
            skLineSegment(sketch, "E221.top", {"start": v(4, 73.83) * mm, "end": v(-69, 73.83) * mm});
            skLineSegment(sketch, "E221.left", {"start": v(4, 335.8) * mm, "end": v(4, 295.8) * mm});
            skLineSegment(sketch, "E221.right", {"start": v(-69, 335.8) * mm, "end": v(-69, 295.8) * mm});
            skLineSegment(sketch, "E222.0.0", {"start": v(0, 181.03) * mm, "end": v(0, 106.27) * mm});
            skLineSegment(sketch, "E222.0.1", {"start": v(0, 106.27) * mm, "end": v(4, 106.27) * mm});
            skLineSegment(sketch, "E222.0.3", {"start": v(4, 181.03) * mm, "end": v(0, 181.03) * mm});
            skLineSegment(sketch, "E222.1.0", {"start": v(0, 295.8) * mm, "end": v(0, 221.03) * mm});
            skLineSegment(sketch, "E222.1.1", {"start": v(0, 221.03) * mm, "end": v(4, 221.03) * mm});
            skLineSegment(sketch, "E222.1.3", {"start": v(4, 295.8) * mm, "end": v(0, 295.8) * mm});
            skLineSegment(sketch, "E222.2.0", {"start": v(-65, 221.03) * mm, "end": v(-65, 295.8) * mm});
            skLineSegment(sketch, "E222.2.1", {"start": v(-65, 295.8) * mm, "end": v(-69, 295.8) * mm});
            skLineSegment(sketch, "E222.2.3", {"start": v(-69, 221.03) * mm, "end": v(-65, 221.03) * mm});
            skLineSegment(sketch, "E222.3.0", {"start": v(-65, 106.27) * mm, "end": v(-65, 181.03) * mm});
            skLineSegment(sketch, "E222.3.1", {"start": v(-65, 181.03) * mm, "end": v(-69, 181.03) * mm});
            skLineSegment(sketch, "E222.3.3", {"start": v(-69, 106.27) * mm, "end": v(-65, 106.27) * mm});
            skLineSegment(sketch, "E223.trimOffspring", {"start": v(4, 221.03) * mm, "end": v(4, 181.03) * mm});
            skLineSegment(sketch, "E224.trimOffspring", {"start": v(4, 106.27) * mm, "end": v(4, 73.83) * mm});
            skLineSegment(sketch, "E225.trimOffspring", {"start": v(-69, 221.03) * mm, "end": v(-69, 181.03) * mm});
            skLineSegment(sketch, "E226.trimOffspring", {"start": v(-69, 106.27) * mm, "end": v(-69, 73.83) * mm});
            skLineSegment(sketch, "E227", {"start": v(-32.5, 335.8) * mm, "end": v(-32.5, 73.83) * mm, "construction": true});
            skCircle(sketch, "E228", {"center": v(-32.5, 284.81) * mm, "radius": 22.5 * mm});
            skArc(sketch, "E229", {"start": v(-10, 204.81) * mm, "mid": v(-32.5, 227.31) * mm, "end": v(-55, 204.81) * mm});
            skArc(sketch, "E230", {"start": v(-55, 124.81) * mm, "mid": v(-32.5, 102.31) * mm, "end": v(-10, 124.81) * mm});
            skLineSegment(sketch, "E231", {"start": v(-55, 124.81) * mm, "end": v(-55, 204.81) * mm});
            skLineSegment(sketch, "E232", {"start": v(-10, 124.81) * mm, "end": v(-10, 204.81) * mm});
            skSolve(sketch);
        }
        {
            var Q0;
            Q0=qSketchRegion(id+"F17",true);
            extrude(context, id + "F18", {"entities" : qUnion([Q0]), "depth" : 4 * mm});
        }
        {
            var Q0;
            Q0=makeQuery(id+"F2.opExtrude","SWEPT_FACE",FACE,{"disambiguationData":[OSD([sQuery(id+"F1.wireOp",EDGE,"E13")])]});
            var sketch = newSketch(context, id + "F19", { "sketchPlane" : qUnion([Q0])});
            skLineSegment(sketch, "E233.bottom", {"start": v(-69.5, 52.3) * mm, "end": v(4, 52.3) * mm});
            skLineSegment(sketch, "E233.top", {"start": v(-69.5, -21.2) * mm, "end": v(4, -21.2) * mm});
            skLineSegment(sketch, "E233.left", {"start": v(-69.5, 52.3) * mm, "end": v(-69.5, -21.2) * mm});
            skLineSegment(sketch, "E233.right", {"start": v(4, 52.3) * mm, "end": v(4, -21.2) * mm});
            skLineSegment(sketch, "E234.bottom", {"start": v(10, -33.2) * mm, "end": v(-75.5, -33.2) * mm});
            skLineSegment(sketch, "E234.top", {"start": v(10, 58.3) * mm, "end": v(-75.5, 58.3) * mm});
            skLineSegment(sketch, "E234.left", {"start": v(10, -33.2) * mm, "end": v(10, 58.3) * mm});
            skLineSegment(sketch, "E234.right", {"start": v(-75.5, -33.2) * mm, "end": v(-75.5, 58.3) * mm});
            skCircle(sketch, "E235", {"center": v(-60.25, -28.2) * mm, "radius": 3 * mm});
            skCircle(sketch, "E236", {"center": v(-5.25, -28.2) * mm, "radius": 3 * mm});
            skLineSegment(sketch, "E237", {"start": v(-32.75, -33.2) * mm, "end": v(-32.75, -21.2) * mm, "construction": true});
            skLineSegment(sketch, "E238", {"start": v(-60.25, -28.2) * mm, "end": v(-32.75, -27.2) * mm, "construction": true});
            skLineSegment(sketch, "E239", {"start": v(-32.75, -27.2) * mm, "end": v(-5.25, -28.2) * mm, "construction": true});
            skSolve(sketch);
        }
        {
            var Q0;
            Q0=qSketchRegion(id+"F19",true);
            extrude(context, id + "F20", {"entities" : qUnion([Q0]), "depth" : 4 * mm});
        }
        {
            var Q0;
            Q0=makeQuery(id+"F6.opExtrude","SWEPT_FACE",FACE,{"disambiguationData":[OSD([sQuery(id+"F5.wireOp",EDGE,"E89.right"),sQuery(id+"F5.wireOp",EDGE,"E90")])]});
            var sketch = newSketch(context, id + "F21", { "sketchPlane" : qUnion([Q0])});
            skPoint(sketch, "E240.visualSharp", {"position": v(-12.49, 26.88) * mm});
            skCircle(sketch, "E241", {"center": v(19.25, 23.09) * mm, "radius": 9.5 * mm});
            skArc(sketch, "E242", {"start": v(19.25, 38.34) * mm, "mid": v(8.37, 33.78) * mm, "end": v(4, 22.81) * mm});
            skLineSegment(sketch, "E243", {"start": v(35.5, 23.09) * mm, "end": v(196.63, 23.09) * mm});
            skLineSegment(sketch, "E244.bottom", {"start": v(37.63, 19.09) * mm, "end": v(57.63, 19.09) * mm});
            skLineSegment(sketch, "E244.top", {"start": v(35.5, -2.91) * mm, "end": v(55.5, -2.91) * mm});
            skLineSegment(sketch, "E244.left", {"start": v(35.5, 16.97) * mm, "end": v(35.5, -2.91) * mm});
            skLineSegment(sketch, "E244.right", {"start": v(57.63, 19.09) * mm, "end": v(57.63, -0.8) * mm});
            skLineSegment(sketch, "E245", {"start": v(35.5, 23.09) * mm, "end": v(35.5, 19.09) * mm, "construction": true});
            skLineSegment(sketch, "E246", {"start": v(35.5, -2.91) * mm, "end": v(35.5, -6.91) * mm, "construction": true});
            skLineSegment(sketch, "E247", {"start": v(35.5, 19.09) * mm, "end": v(57.63, -2.91) * mm, "construction": true});
            skLineSegment(sketch, "E248", {"start": v(37.63, 19.09) * mm, "end": v(57.63, -0.8) * mm});
            skLineSegment(sketch, "E249", {"start": v(55.5, -2.91) * mm, "end": v(35.5, 16.97) * mm});
            skLineSegment(sketch, "E250.1.0.0", {"start": v(82.5, -2.91) * mm, "end": v(62.5, 16.97) * mm});
            skLineSegment(sketch, "E250.1.0.1", {"start": v(84.63, 19.09) * mm, "end": v(84.63, -0.8) * mm});
            skLineSegment(sketch, "E250.1.0.2", {"start": v(62.5, 16.97) * mm, "end": v(62.5, -2.91) * mm});
            skLineSegment(sketch, "E250.1.0.3", {"start": v(62.5, -2.91) * mm, "end": v(62.5, -6.91) * mm, "construction": true});
            skLineSegment(sketch, "E250.1.0.4", {"start": v(62.5, 19.09) * mm, "end": v(84.63, -2.91) * mm, "construction": true});
            skLineSegment(sketch, "E250.1.0.5", {"start": v(64.63, 19.09) * mm, "end": v(84.63, 19.09) * mm});
            skLineSegment(sketch, "E250.1.0.6", {"start": v(62.5, -2.91) * mm, "end": v(82.5, -2.91) * mm});
            skLineSegment(sketch, "E250.1.0.7", {"start": v(64.63, 19.09) * mm, "end": v(84.63, -0.8) * mm});
            skLineSegment(sketch, "E250.1.0.8", {"start": v(62.5, 23.09) * mm, "end": v(62.5, 19.09) * mm, "construction": true});
            skLineSegment(sketch, "E250.2.0.0", {"start": v(109.5, -2.91) * mm, "end": v(89.5, 16.97) * mm});
            skLineSegment(sketch, "E250.2.0.1", {"start": v(111.63, 19.09) * mm, "end": v(111.63, -0.8) * mm});
            skLineSegment(sketch, "E250.2.0.2", {"start": v(89.5, 16.97) * mm, "end": v(89.5, -2.91) * mm});
            skLineSegment(sketch, "E250.2.0.3", {"start": v(89.5, -2.91) * mm, "end": v(89.5, -6.91) * mm, "construction": true});
            skLineSegment(sketch, "E250.2.0.4", {"start": v(89.5, 19.09) * mm, "end": v(111.63, -2.91) * mm, "construction": true});
            skLineSegment(sketch, "E250.2.0.5", {"start": v(91.63, 19.09) * mm, "end": v(111.63, 19.09) * mm});
            skLineSegment(sketch, "E250.2.0.6", {"start": v(89.5, -2.91) * mm, "end": v(109.5, -2.91) * mm});
            skLineSegment(sketch, "E250.2.0.7", {"start": v(91.63, 19.09) * mm, "end": v(111.63, -0.8) * mm});
            skLineSegment(sketch, "E250.2.0.8", {"start": v(89.5, 23.09) * mm, "end": v(89.5, 19.09) * mm, "construction": true});
            skLineSegment(sketch, "E250.3.0.0", {"start": v(136.5, -2.91) * mm, "end": v(116.5, 16.97) * mm});
            skLineSegment(sketch, "E250.3.0.1", {"start": v(138.63, 19.09) * mm, "end": v(138.63, -0.8) * mm});
            skLineSegment(sketch, "E250.3.0.2", {"start": v(116.5, 16.97) * mm, "end": v(116.5, -2.91) * mm});
            skLineSegment(sketch, "E250.3.0.3", {"start": v(116.5, -2.91) * mm, "end": v(116.5, -6.91) * mm, "construction": true});
            skLineSegment(sketch, "E250.3.0.4", {"start": v(116.5, 19.09) * mm, "end": v(138.63, -2.91) * mm, "construction": true});
            skLineSegment(sketch, "E250.3.0.5", {"start": v(118.63, 19.09) * mm, "end": v(138.63, 19.09) * mm});
            skLineSegment(sketch, "E250.3.0.6", {"start": v(116.5, -2.91) * mm, "end": v(136.5, -2.91) * mm});
            skLineSegment(sketch, "E250.3.0.7", {"start": v(118.63, 19.09) * mm, "end": v(138.63, -0.8) * mm});
            skLineSegment(sketch, "E250.3.0.8", {"start": v(116.5, 23.09) * mm, "end": v(116.5, 19.09) * mm, "construction": true});
            skLineSegment(sketch, "E250.4.0.0", {"start": v(163.5, -2.91) * mm, "end": v(143.5, 16.97) * mm});
            skLineSegment(sketch, "E250.4.0.1", {"start": v(165.63, 19.09) * mm, "end": v(165.63, -0.8) * mm});
            skLineSegment(sketch, "E250.4.0.2", {"start": v(143.5, 16.97) * mm, "end": v(143.5, -2.91) * mm});
            skLineSegment(sketch, "E250.4.0.3", {"start": v(143.5, -2.91) * mm, "end": v(143.5, -6.91) * mm, "construction": true});
            skLineSegment(sketch, "E250.4.0.4", {"start": v(143.5, 19.09) * mm, "end": v(165.63, -2.91) * mm, "construction": true});
            skLineSegment(sketch, "E250.4.0.5", {"start": v(145.63, 19.09) * mm, "end": v(165.63, 19.09) * mm});
            skLineSegment(sketch, "E250.4.0.6", {"start": v(143.5, -2.91) * mm, "end": v(163.5, -2.91) * mm});
            skLineSegment(sketch, "E250.4.0.7", {"start": v(145.63, 19.09) * mm, "end": v(165.63, -0.8) * mm});
            skLineSegment(sketch, "E250.4.0.8", {"start": v(143.5, 23.09) * mm, "end": v(143.5, 19.09) * mm, "construction": true});
            skLineSegment(sketch, "E250.5.0.0", {"start": v(190.5, -2.91) * mm, "end": v(170.5, 16.97) * mm});
            skLineSegment(sketch, "E250.5.0.1", {"start": v(192.63, 19.09) * mm, "end": v(192.63, -0.8) * mm});
            skLineSegment(sketch, "E250.5.0.2", {"start": v(170.5, 16.97) * mm, "end": v(170.5, -2.91) * mm});
            skLineSegment(sketch, "E250.5.0.3", {"start": v(170.5, -2.91) * mm, "end": v(170.5, -6.91) * mm, "construction": true});
            skLineSegment(sketch, "E250.5.0.4", {"start": v(170.5, 19.09) * mm, "end": v(192.63, -2.91) * mm, "construction": true});
            skLineSegment(sketch, "E250.5.0.5", {"start": v(172.63, 19.09) * mm, "end": v(192.63, 19.09) * mm});
            skLineSegment(sketch, "E250.5.0.6", {"start": v(170.5, -2.91) * mm, "end": v(190.5, -2.91) * mm});
            skLineSegment(sketch, "E250.5.0.7", {"start": v(172.63, 19.09) * mm, "end": v(192.63, -0.8) * mm});
            skLineSegment(sketch, "E250.5.0.8", {"start": v(170.5, 23.09) * mm, "end": v(170.5, 19.09) * mm, "construction": true});
            skLineSegment(sketch, "E250.direction1", {"start": v(35.5, 16.97) * mm, "end": v(62.5, 16.97) * mm, "construction": true});
            skLineSegment(sketch, "E251", {"start": v(196.63, 23.09) * mm, "end": v(196.63, -6.91) * mm, "construction": true});
            skLineSegment(sketch, "E252", {"start": v(196.63, -6.91) * mm, "end": v(-32.5, -6.91) * mm});
            skArc(sketch, "E253", {"start": v(-34.5, 0.55) * mm, "mid": v(-36.36, -3.95) * mm, "end": v(-32.5, -6.91) * mm});
            skLineSegment(sketch, "E254", {"start": v(4, 22.81) * mm, "end": v(-34.5, 0.55) * mm});
            skLineSegment(sketch, "E255", {"start": v(196.63, -6.91) * mm, "end": v(239.4, -6.91) * mm});
            skCircle(sketch, "E256", {"center": v(19.25, 23.09) * mm, "radius": 5 * mm, "construction": true});
            skCircle(sketch, "E257", {"center": v(11.5, 10.83) * mm, "radius": 2.5 * mm});
            skCircle(sketch, "E258", {"center": v(27, 35.34) * mm, "radius": 2.5 * mm});
            skLineSegment(sketch, "E259", {"start": v(27, 35.34) * mm, "end": v(11.5, 10.83) * mm, "construction": true});
            skCircle(sketch, "E260", {"center": v(27, 35.34) * mm, "radius": 7.5 * mm, "construction": true});
            skCircle(sketch, "E261", {"center": v(11.5, 10.83) * mm, "radius": 7.5 * mm, "construction": true});
            skPoint(sketch, "E262", {"position": v(59.3, 23.09) * mm});
            skArc(sketch, "E263", {"start": v(59.3, 23.09) * mm, "mid": v(44.53, 44.51) * mm, "end": v(19.25, 38.34) * mm});
            skLineSegment(sketch, "E264", {"start": v(196.63, 23.09) * mm, "end": v(240.44, -3.2) * mm});
            skPoint(sketch, "E265.visualSharp", {"position": v(246.63, -6.91) * mm});
            skArc(sketch, "E265.filletArc", {"start": v(239.4, -6.91) * mm, "mid": v(241.33, -5.44) * mm, "end": v(240.44, -3.2) * mm});
            skLineSegment(sketch, "E266", {"start": v(196.63, 19.09) * mm, "end": v(227.1, 0.8) * mm});
            skLineSegment(sketch, "E267", {"start": v(226.07, -2.91) * mm, "end": v(196.63, -2.91) * mm});
            skLineSegment(sketch, "E268", {"start": v(196.63, -2.91) * mm, "end": v(196.63, 19.09) * mm});
            skPoint(sketch, "E269.visualSharp", {"position": v(233.3, -2.91) * mm});
            skArc(sketch, "E269.filletArc", {"start": v(226.07, -2.91) * mm, "mid": v(228, -1.44) * mm, "end": v(227.1, 0.8) * mm});
            skSolve(sketch);
        }
        {
            var Q0;
            Q0=qSketchRegion(id+"F21",true);
            extrude(context, id + "F22", {"entities" : qUnion([Q0]), "depth" : 4 * mm});
        }
        {
            var Q0;
            Q0=makeQuery(id+"F6.opExtrude","SWEPT_FACE",FACE,{"disambiguationData":[OSD([sQuery(id+"F5.wireOp",EDGE,"E108.left")])]});
            var sketch = newSketch(context, id + "F23", { "sketchPlane" : qUnion([Q0])});
            skLineSegment(sketch, "E270", {"start": v(-4, 40.73) * mm, "end": v(0, 40.73) * mm});
            skLineSegment(sketch, "E271", {"start": v(0, 40.73) * mm, "end": v(0, 20.73) * mm});
            skLineSegment(sketch, "E272", {"start": v(0, 20.73) * mm, "end": v(-4, 20.73) * mm});
            skLineSegment(sketch, "E273", {"start": v(-4, 20.73) * mm, "end": v(-4, 12.73) * mm});
            skLineSegment(sketch, "E274", {"start": v(-4, 12.73) * mm, "end": v(0, 12.73) * mm});
            skLineSegment(sketch, "E275", {"start": v(0, 12.73) * mm, "end": v(0, -7.27) * mm});
            skLineSegment(sketch, "E276", {"start": v(0, -7.27) * mm, "end": v(-4, -7.27) * mm});
            skLineSegment(sketch, "E277", {"start": v(-4, -7.27) * mm, "end": v(-4, -17.3) * mm});
            skLineSegment(sketch, "E278", {"start": v(-4, -17.3) * mm, "end": v(-24, -17.3) * mm});
            skLineSegment(sketch, "E279", {"start": v(-39, -2.3) * mm, "end": v(-39, 33.07) * mm});
            skLineSegment(sketch, "E280", {"start": v(-24, 48.07) * mm, "end": v(-4, 48.07) * mm});
            skLineSegment(sketch, "E281", {"start": v(-4, 48.07) * mm, "end": v(-4, 40.73) * mm});
            skPoint(sketch, "E282.visualSharp", {"position": v(-39, 48.07) * mm});
            skArc(sketch, "E282.filletArc", {"start": v(-24, 48.07) * mm, "mid": v(-34.6, 43.67) * mm, "end": v(-39, 33.07) * mm});
            skPoint(sketch, "E283.visualSharp", {"position": v(-39, -17.3) * mm});
            skArc(sketch, "E283.filletArc", {"start": v(-39, -2.3) * mm, "mid": v(-34.6, -12.9) * mm, "end": v(-24, -17.3) * mm});
            skCircle(sketch, "E284", {"center": v(-19.25, 23.09) * mm, "radius": 2.5 * mm});
            skSolve(sketch);
        }
        {
            var Q0;
            Q0=qSketchRegion(id+"F23",true);
            extrude(context, id + "F24", {"entities" : qUnion([Q0]), "depth" : 4 * mm});
        }
        {
            var Q0;
            Q0=makeQuery(id+"F8.opExtrude","CAP_FACE",FACE,{"disambiguationData":[OSD([sQuery(id+"F7.wireOp",EDGE,"E125"),sQuery(id+"F7.wireOp",EDGE,"E126"),sQuery(id+"F7.wireOp",EDGE,"E127"),sQuery(id+"F7.wireOp",EDGE,"E128.0.0"),sQuery(id+"F7.wireOp",EDGE,"E128.0.3"),sQuery(id+"F7.wireOp",EDGE,"E129.0.0"),sQuery(id+"F7.wireOp",EDGE,"E129.0.1"),sQuery(id+"F7.wireOp",EDGE,"E129.0.3"),sQuery(id+"F7.wireOp",EDGE,"E130.trimOffspring"),sQuery(id+"F7.wireOp",EDGE,"E131.0.0"),sQuery(id+"F7.wireOp",EDGE,"E131.0.1"),sQuery(id+"F7.wireOp",EDGE,"E131.0.3"),sQuery(id+"F7.wireOp",EDGE,"E132.trimOffspring"),sQuery(id+"F7.wireOp",EDGE,"E133.0.0"),sQuery(id+"F7.wireOp",EDGE,"E133.0.1"),sQuery(id+"F7.wireOp",EDGE,"E134"),sQuery(id+"F7.wireOp",EDGE,"E136.0.MirrorCS"),sQuery(id+"F7.wireOp",EDGE,"E137.0.MirrorCS"),sQuery(id+"F7.wireOp",EDGE,"E138.0.MirrorCS"),sQuery(id+"F7.wireOp",EDGE,"E139.0.MirrorCS"),sQuery(id+"F7.wireOp",EDGE,"E140.0.MirrorCS"),sQuery(id+"F7.wireOp",EDGE,"E141.0.MirrorCS"),sQuery(id+"F7.wireOp",EDGE,"E142.0.MirrorCS"),sQuery(id+"F7.wireOp",EDGE,"E143.0.MirrorCS"),sQuery(id+"F7.wireOp",EDGE,"E144.trimOffspring"),sQuery(id+"F7.wireOp",EDGE,"E145.trimOffspring"),sQuery(id+"F7.wireOp",EDGE,"E146.trimOffspring"),sQuery(id+"F7.wireOp",EDGE,"E147"),sQuery(id+"F7.wireOp",EDGE,"E148"),sQuery(id+"F7.wireOp",EDGE,"E149"),sQuery(id+"F7.wireOp",EDGE,"E150.trimOffspring"),sQuery(id+"F7.wireOp",EDGE,"E151.bottom"),sQuery(id+"F7.wireOp",EDGE,"E151.top"),sQuery(id+"F7.wireOp",EDGE,"E151.right"),sQuery(id+"F7.wireOp",EDGE,"E152.trimOffspring"),sQuery(id+"F7.wireOp",EDGE,"E153"),sQuery(id+"F7.wireOp",EDGE,"E154"),sQuery(id+"F7.wireOp",EDGE,"E156"),sQuery(id+"F7.wireOp",EDGE,"E157"),sQuery(id+"F7.wireOp",EDGE,"E158")])],"isStart":false});
            var sketch = newSketch(context, id + "F25", { "sketchPlane" : qUnion([Q0])});
            skLineSegment(sketch, "E285.bottom", {"start": v(-65, -440.56) * mm, "end": v(-59, -440.56) * mm});
            skLineSegment(sketch, "E285.top", {"start": v(-65, -450.56) * mm, "end": v(-59, -450.56) * mm});
            skLineSegment(sketch, "E285.left", {"start": v(-65, -440.56) * mm, "end": v(-65, -450.56) * mm});
            skLineSegment(sketch, "E285.right", {"start": v(-59, -440.56) * mm, "end": v(-59, -450.56) * mm});
            skSolve(sketch);
        }
        {
            var Q0;
            Q0=qSketchRegion(id+"F25",true);
            extrude(context, id + "F26", {"entities" : qUnion([Q0]), "operationType" : NewBodyOperationType.REMOVE, "oppositeDirection" : true, "depth" : 25 * mm});
        }
        {
            var Q0;
            Q0=makeQuery(id+"F8.opExtrude","CAP_FACE",FACE,{"disambiguationData":[OSD([sQuery(id+"F7.wireOp",EDGE,"E125"),sQuery(id+"F7.wireOp",EDGE,"E126"),sQuery(id+"F7.wireOp",EDGE,"E127"),sQuery(id+"F7.wireOp",EDGE,"E128.0.0"),sQuery(id+"F7.wireOp",EDGE,"E128.0.3"),sQuery(id+"F7.wireOp",EDGE,"E129.0.0"),sQuery(id+"F7.wireOp",EDGE,"E129.0.1"),sQuery(id+"F7.wireOp",EDGE,"E129.0.3"),sQuery(id+"F7.wireOp",EDGE,"E130.trimOffspring"),sQuery(id+"F7.wireOp",EDGE,"E131.0.0"),sQuery(id+"F7.wireOp",EDGE,"E131.0.1"),sQuery(id+"F7.wireOp",EDGE,"E131.0.3"),sQuery(id+"F7.wireOp",EDGE,"E132.trimOffspring"),sQuery(id+"F7.wireOp",EDGE,"E133.0.0"),sQuery(id+"F7.wireOp",EDGE,"E133.0.1"),sQuery(id+"F7.wireOp",EDGE,"E134"),sQuery(id+"F7.wireOp",EDGE,"E136.0.MirrorCS"),sQuery(id+"F7.wireOp",EDGE,"E137.0.MirrorCS"),sQuery(id+"F7.wireOp",EDGE,"E138.0.MirrorCS"),sQuery(id+"F7.wireOp",EDGE,"E139.0.MirrorCS"),sQuery(id+"F7.wireOp",EDGE,"E140.0.MirrorCS"),sQuery(id+"F7.wireOp",EDGE,"E141.0.MirrorCS"),sQuery(id+"F7.wireOp",EDGE,"E142.0.MirrorCS"),sQuery(id+"F7.wireOp",EDGE,"E143.0.MirrorCS"),sQuery(id+"F7.wireOp",EDGE,"E144.trimOffspring"),sQuery(id+"F7.wireOp",EDGE,"E145.trimOffspring"),sQuery(id+"F7.wireOp",EDGE,"E146.trimOffspring"),sQuery(id+"F7.wireOp",EDGE,"E147"),sQuery(id+"F7.wireOp",EDGE,"E148"),sQuery(id+"F7.wireOp",EDGE,"E149"),sQuery(id+"F7.wireOp",EDGE,"E150.trimOffspring"),sQuery(id+"F7.wireOp",EDGE,"E151.bottom"),sQuery(id+"F7.wireOp",EDGE,"E151.top"),sQuery(id+"F7.wireOp",EDGE,"E151.right"),sQuery(id+"F7.wireOp",EDGE,"E152.trimOffspring"),sQuery(id+"F7.wireOp",EDGE,"E153"),sQuery(id+"F7.wireOp",EDGE,"E154"),sQuery(id+"F7.wireOp",EDGE,"E156"),sQuery(id+"F7.wireOp",EDGE,"E157"),sQuery(id+"F7.wireOp",EDGE,"E158")])],"isStart":false});
            var sketch = newSketch(context, id + "F27", { "sketchPlane" : qUnion([Q0])});
            skLineSegment(sketch, "E286.bottom", {"start": v(0, -67.8) * mm, "end": v(-32.5, -67.8) * mm});
            skLineSegment(sketch, "E286.top", {"start": v(0, -66.7) * mm, "end": v(-32.5, -66.7) * mm});
            skLineSegment(sketch, "E286.left", {"start": v(0, -67.8) * mm, "end": v(0, -66.7) * mm});
            skLineSegment(sketch, "E286.right", {"start": v(-32.5, -67.8) * mm, "end": v(-32.5, -66.7) * mm});
            skSolve(sketch);
        }
        {
            var Q0;
            Q0=qSketchRegion(id+"F27",true);
            extrude(context, id + "F28", {"entities" : qUnion([Q0]), "operationType" : NewBodyOperationType.REMOVE, "oppositeDirection" : true, "depth" : 25 * mm});
        }
        {
            var Q0;
            Q0=makeQuery(id+"F10.opExtrude","SWEPT_BODY",BODY,{"disambiguationData":[OSD([sQuery(id+"F9.wireOp",EDGE,"E161.0.0"),sQuery(id+"F9.wireOp",EDGE,"E161.0.37"),sQuery(id+"F9.wireOp",EDGE,"E161.0.38"),sQuery(id+"F9.wireOp",EDGE,"E161.0.39"),sQuery(id+"F9.wireOp",EDGE,"E161.0.40"),sQuery(id+"F9.wireOp",EDGE,"E161.0.41"),sQuery(id+"F9.wireOp",EDGE,"E172")])]});
            deleteBodies(context, id + "F29", {"entities" : qUnion([Q0])});
        }
        {
            var Q0;
            Q0=makeQuery(id+"F22.opExtrude","CAP_FACE",FACE,{"disambiguationData":[OSD([sQuery(id+"F21.wireOp",EDGE,"E241"),sQuery(id+"F21.wireOp",EDGE,"E242"),sQuery(id+"F21.wireOp",EDGE,"E243"),sQuery(id+"F21.wireOp",EDGE,"E244.bottom"),sQuery(id+"F21.wireOp",EDGE,"E244.top"),sQuery(id+"F21.wireOp",EDGE,"E244.left"),sQuery(id+"F21.wireOp",EDGE,"E244.right"),sQuery(id+"F21.wireOp",EDGE,"E248"),sQuery(id+"F21.wireOp",EDGE,"E249"),sQuery(id+"F21.wireOp",EDGE,"E250.1.0.0"),sQuery(id+"F21.wireOp",EDGE,"E250.1.0.1"),sQuery(id+"F21.wireOp",EDGE,"E250.1.0.2"),sQuery(id+"F21.wireOp",EDGE,"E250.1.0.5"),sQuery(id+"F21.wireOp",EDGE,"E250.1.0.6"),sQuery(id+"F21.wireOp",EDGE,"E250.1.0.7"),sQuery(id+"F21.wireOp",EDGE,"E250.2.0.0"),sQuery(id+"F21.wireOp",EDGE,"E250.2.0.1"),sQuery(id+"F21.wireOp",EDGE,"E250.2.0.2"),sQuery(id+"F21.wireOp",EDGE,"E250.2.0.5"),sQuery(id+"F21.wireOp",EDGE,"E250.2.0.6"),sQuery(id+"F21.wireOp",EDGE,"E250.2.0.7"),sQuery(id+"F21.wireOp",EDGE,"E250.3.0.0"),sQuery(id+"F21.wireOp",EDGE,"E250.3.0.1"),sQuery(id+"F21.wireOp",EDGE,"E250.3.0.2"),sQuery(id+"F21.wireOp",EDGE,"E250.3.0.5"),sQuery(id+"F21.wireOp",EDGE,"E250.3.0.6"),sQuery(id+"F21.wireOp",EDGE,"E250.3.0.7"),sQuery(id+"F21.wireOp",EDGE,"E250.4.0.0"),sQuery(id+"F21.wireOp",EDGE,"E250.4.0.1"),sQuery(id+"F21.wireOp",EDGE,"E250.4.0.2"),sQuery(id+"F21.wireOp",EDGE,"E250.4.0.5"),sQuery(id+"F21.wireOp",EDGE,"E250.4.0.6"),sQuery(id+"F21.wireOp",EDGE,"E250.4.0.7"),sQuery(id+"F21.wireOp",EDGE,"E250.5.0.0"),sQuery(id+"F21.wireOp",EDGE,"E250.5.0.1"),sQuery(id+"F21.wireOp",EDGE,"E250.5.0.2"),sQuery(id+"F21.wireOp",EDGE,"E250.5.0.5"),sQuery(id+"F21.wireOp",EDGE,"E250.5.0.6"),sQuery(id+"F21.wireOp",EDGE,"E250.5.0.7"),sQuery(id+"F21.wireOp",EDGE,"E252"),sQuery(id+"F21.wireOp",EDGE,"E253"),sQuery(id+"F21.wireOp",EDGE,"E254"),sQuery(id+"F21.wireOp",EDGE,"E255"),sQuery(id+"F21.wireOp",EDGE,"E257"),sQuery(id+"F21.wireOp",EDGE,"E258"),sQuery(id+"F21.wireOp",EDGE,"E263"),sQuery(id+"F21.wireOp",EDGE,"E264"),sQuery(id+"F21.wireOp",EDGE,"E265.filletArc")])],"isStart":false});
            var sketch = newSketch(context, id + "F30", { "sketchPlane" : qUnion([Q0])});
            skLineSegment(sketch, "E287", {"start": v(14.29, -6.91) * mm, "end": v(14.29, -21.91) * mm});
            skLineSegment(sketch, "E288", {"start": v(14.29, -21.91) * mm, "end": v(249.97, -21.91) * mm});
            skArc(sketch, "E289", {"start": v(249.97, -21.91) * mm, "mid": v(255.75, -17.51) * mm, "end": v(253.05, -10.77) * mm});
            skLineSegment(sketch, "E290", {"start": v(14.29, -6.91) * mm, "end": v(239.4, -6.91) * mm});
            skArc(sketch, "E291.0", {"start": v(239.4, -6.91) * mm, "mid": v(241.33, -5.44) * mm, "end": v(240.44, -3.2) * mm});
            skLineSegment(sketch, "E292", {"start": v(253.05, -10.77) * mm, "end": v(240.44, -3.2) * mm});
            skSolve(sketch);
        }
        {
            var Q0;
            Q0=qSketchRegion(id+"F30",true);
            extrude(context, id + "F31", {"entities" : qUnion([Q0]), "operationType" : NewBodyOperationType.ADD, "oppositeDirection" : true, "depth" : 4 * mm});
        }
        {
            var Q0;
            Q0=makeQuery(id+"F31.opExtrude","SWEPT_EDGE",EDGE,{"disambiguationData":[OSD([sQuery(id+"F30.wireOp",EDGE,"E287"),sQuery(id+"F30.wireOp",EDGE,"E288")])]});
            fillet(context, id + "F32", {"entities" : qUnion([Q0]), "radius" : 20 * mm, "tangentPropagation" : true, "allowEdgeOverflow" : false});
        }
    });
